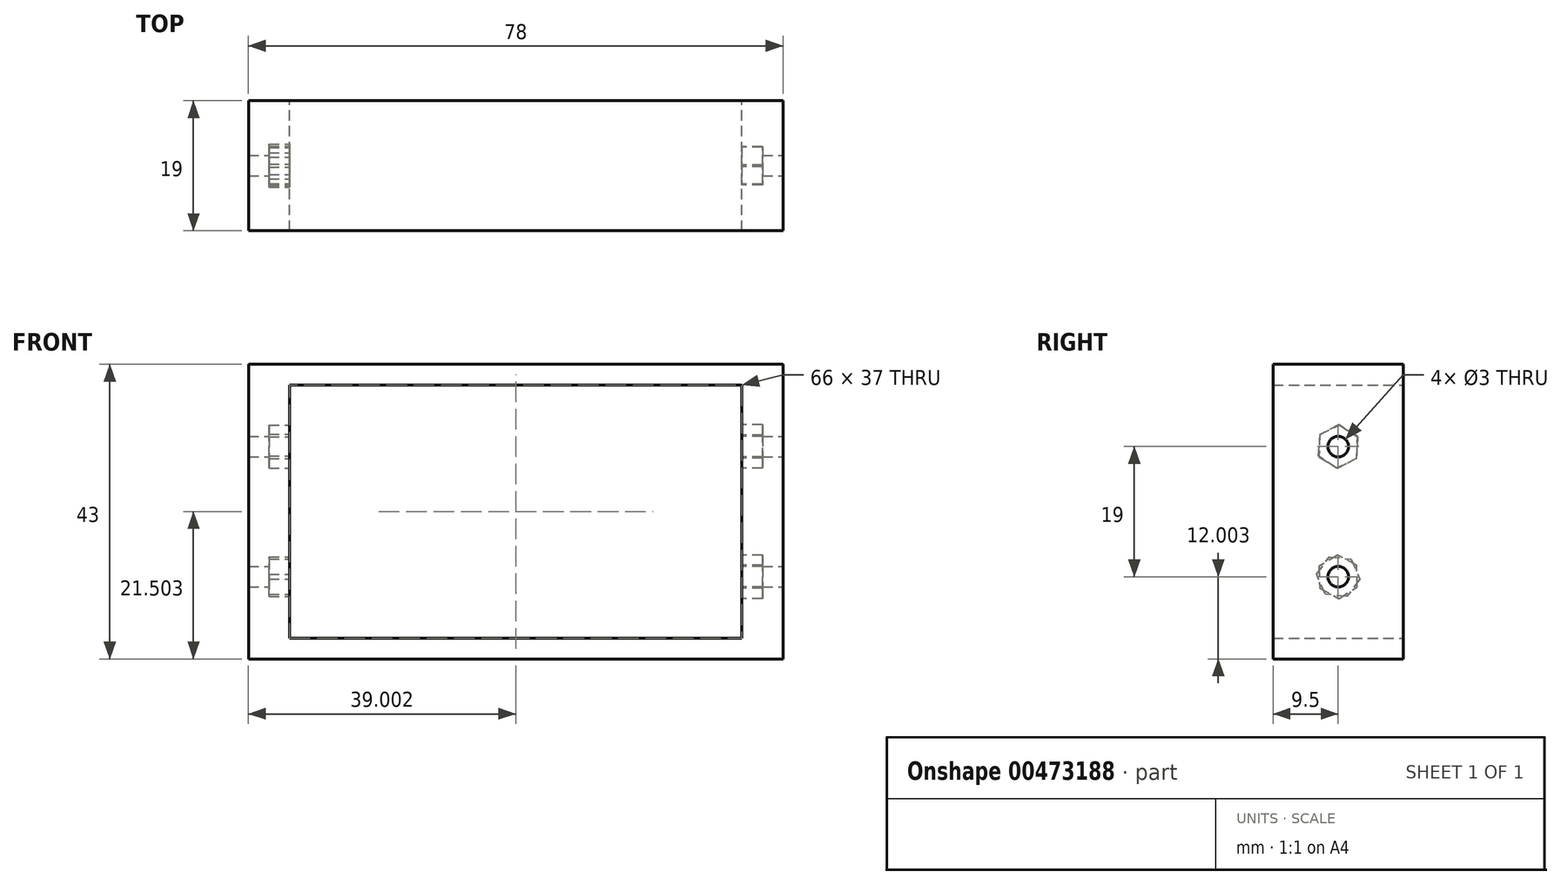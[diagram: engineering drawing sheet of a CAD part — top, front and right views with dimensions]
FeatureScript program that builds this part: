
annotation { "Feature Type Name" : "Feature", "Feature Type Description" : "" }
export const myFeature = defineFeature(function(context is Context, id is Id, definition is map)
    precondition{}
    {
        {
            var Q0;
            Q0=qCreatedBy(makeId("Front.planeOp"),FACE);
            var sketch = newSketch(context, id + "F0", { "sketchPlane" : qUnion([Q0])});
            skLineSegment(sketch, "E0.bottom", {"start": v(-26.52, 20.57) * mm, "end": v(51.48, 20.57) * mm});
            skLineSegment(sketch, "E0.top", {"start": v(-26.52, -22.43) * mm, "end": v(51.48, -22.43) * mm});
            skLineSegment(sketch, "E0.left", {"start": v(-26.52, 20.57) * mm, "end": v(-26.52, -22.43) * mm});
            skLineSegment(sketch, "E0.right", {"start": v(51.48, 20.57) * mm, "end": v(51.48, -22.43) * mm});
            skLineSegment(sketch, "E1.bottom", {"start": v(-20.52, 17.57) * mm, "end": v(45.48, 17.57) * mm});
            skLineSegment(sketch, "E1.top", {"start": v(-20.52, -19.43) * mm, "end": v(45.48, -19.43) * mm});
            skLineSegment(sketch, "E1.left", {"start": v(-20.52, 17.57) * mm, "end": v(-20.52, -19.43) * mm});
            skLineSegment(sketch, "E1.right", {"start": v(45.48, 17.57) * mm, "end": v(45.48, -19.43) * mm});
            skSolve(sketch);
        }
        {
            var Q0;
            Q0=makeQuery(id+"F0.imprint","IMPRINT",FACE,{"disambiguationData":[TD([[makeQuery(id+"F0.imprint","IMPRINT",EDGE,{"derivedFrom":sQuery(id+"F0.wireOp",EDGE,"E0.bottom")}),-1.0]])]});
            extrude(context, id + "F1", {"entities" : qUnion([Q0]), "depth" : 19 * mm});
        }
        {
            var Q0;
            Q0=makeQuery(id+"F1.opExtrude","SWEPT_FACE",FACE,{"disambiguationData":[OSD([sQuery(id+"F0.wireOp",EDGE,"E0.right")])]});
            var sketch = newSketch(context, id + "F2", { "sketchPlane" : qUnion([Q0])});
            skCircle(sketch, "E2", {"center": v(-9.5, 8.57) * mm, "radius": 1.5 * mm});
            skCircle(sketch, "E3", {"center": v(-9.5, -10.43) * mm, "radius": 1.5 * mm});
            skSolve(sketch);
        }
        {
            var Q0;
            Q0=makeQuery(id+"F2.imprint","IMPRINT",FACE,{"disambiguationData":[TD([[makeQuery(id+"F2.imprint","IMPRINT",EDGE,{"derivedFrom":sQuery(id+"F2.wireOp",EDGE,"E2")}),1.0]])]});
            var Q1;
            Q1=makeQuery(id+"F2.imprint","IMPRINT",FACE,{"disambiguationData":[TD([[makeQuery(id+"F2.imprint","IMPRINT",EDGE,{"derivedFrom":sQuery(id+"F2.wireOp",EDGE,"E3")}),1.0]])]});
            extrude(context, id + "F3", {"entities" : qUnion([Q0, Q1]), "operationType" : NewBodyOperationType.REMOVE, "oppositeDirection" : true, "depth" : 78 * mm, "offsetDistance" : 25 * mm});
        }
        {
            var Q0;
            Q0=makeQuery(id+"F1.opExtrude","SWEPT_FACE",FACE,{"disambiguationData":[OSD([sQuery(id+"F0.wireOp",EDGE,"E1.left")])]});
            var sketch = newSketch(context, id + "F4", { "sketchPlane" : qUnion([Q0])});
            skCircle(sketch, "E4.cCircle", {"center": v(-9.5, 8.57) * mm, "radius": 2.75 * mm, "construction": true});
            skLineSegment(sketch, "E4.0", {"start": v(-9.28, 11.74) * mm, "end": v(-6.65, 9.97) * mm});
            skLineSegment(sketch, "E4.1", {"start": v(-6.65, 9.97) * mm, "end": v(-6.87, 6.8) * mm});
            skLineSegment(sketch, "E4.2", {"start": v(-6.87, 6.8) * mm, "end": v(-9.72, 5.4) * mm});
            skLineSegment(sketch, "E4.3", {"start": v(-9.72, 5.4) * mm, "end": v(-12.35, 7.18) * mm});
            skLineSegment(sketch, "E4.4", {"start": v(-12.35, 7.18) * mm, "end": v(-12.13, 10.35) * mm});
            skLineSegment(sketch, "E4.5", {"start": v(-12.13, 10.35) * mm, "end": v(-9.28, 11.74) * mm});
            skPoint(sketch, "E4.0.midPoint", {"position": v(-7.96, 10.85) * mm});
            skCircle(sketch, "E5.cCircle", {"center": v(-9.5, -10.43) * mm, "radius": 2.75 * mm, "construction": true});
            skLineSegment(sketch, "E5.0", {"start": v(-10.77, -7.51) * mm, "end": v(-7.61, -7.87) * mm});
            skLineSegment(sketch, "E5.1", {"start": v(-7.61, -7.87) * mm, "end": v(-6.35, -10.79) * mm});
            skLineSegment(sketch, "E5.2", {"start": v(-6.35, -10.79) * mm, "end": v(-8.23, -13.34) * mm});
            skLineSegment(sketch, "E5.3", {"start": v(-8.23, -13.34) * mm, "end": v(-11.39, -12.98) * mm});
            skLineSegment(sketch, "E5.4", {"start": v(-11.39, -12.98) * mm, "end": v(-12.65, -10.07) * mm});
            skLineSegment(sketch, "E5.5", {"start": v(-12.65, -10.07) * mm, "end": v(-10.77, -7.51) * mm});
            skPoint(sketch, "E5.0.midPoint", {"position": v(-9.19, -7.7) * mm});
            skSolve(sketch);
        }
        {
            var Q0;
            Q0 = qSketchRegion(id + "F4", true);
            extrude(context, id + "F5", {"entities" : qUnion([Q0]), "operationType" : NewBodyOperationType.REMOVE, "oppositeDirection" : true, "depth" : 3 * mm});
        }
        {
            var Q0;
            Q0=makeQuery(id+"F1.opExtrude","SWEPT_FACE",FACE,{"disambiguationData":[OSD([sQuery(id+"F0.wireOp",EDGE,"E1.right")])]});
            var sketch = newSketch(context, id + "F6", { "sketchPlane" : qUnion([Q0])});
            skCircle(sketch, "E6.cCircle", {"center": v(9.5, 8.57) * mm, "radius": 2.75 * mm, "construction": true});
            skLineSegment(sketch, "E6.0", {"start": v(12.3, 7.08) * mm, "end": v(9.6, 5.4) * mm});
            skLineSegment(sketch, "E6.1", {"start": v(9.6, 5.4) * mm, "end": v(6.8, 6.9) * mm});
            skLineSegment(sketch, "E6.2", {"start": v(6.8, 6.9) * mm, "end": v(6.7, 10.07) * mm});
            skLineSegment(sketch, "E6.3", {"start": v(6.7, 10.07) * mm, "end": v(9.4, 11.75) * mm});
            skLineSegment(sketch, "E6.4", {"start": v(9.4, 11.75) * mm, "end": v(12.2, 10.25) * mm});
            skLineSegment(sketch, "E6.5", {"start": v(12.2, 10.25) * mm, "end": v(12.3, 7.08) * mm});
            skPoint(sketch, "E6.0.midPoint", {"position": v(10.96, 6.24) * mm});
            skCircle(sketch, "E7.cCircle", {"center": v(9.5, -10.43) * mm, "radius": 2.75 * mm, "construction": true});
            skLineSegment(sketch, "E7.0", {"start": v(12.2, -12.1) * mm, "end": v(9.4, -13.6) * mm});
            skLineSegment(sketch, "E7.1", {"start": v(9.4, -13.6) * mm, "end": v(6.7, -11.93) * mm});
            skLineSegment(sketch, "E7.2", {"start": v(6.7, -11.93) * mm, "end": v(6.8, -8.75) * mm});
            skLineSegment(sketch, "E7.3", {"start": v(6.8, -8.75) * mm, "end": v(9.6, -7.25) * mm});
            skLineSegment(sketch, "E7.4", {"start": v(9.6, -7.25) * mm, "end": v(12.3, -8.93) * mm});
            skLineSegment(sketch, "E7.5", {"start": v(12.3, -8.93) * mm, "end": v(12.2, -12.1) * mm});
            skPoint(sketch, "E7.0.midPoint", {"position": v(10.8, -12.85) * mm});
            skSolve(sketch);
        }
        {
            var Q0;
            Q0 = qSketchRegion(id + "F6", true);
            extrude(context, id + "F7", {"entities" : qUnion([Q0]), "operationType" : NewBodyOperationType.REMOVE, "oppositeDirection" : true, "depth" : 3 * mm});
        }
    });
